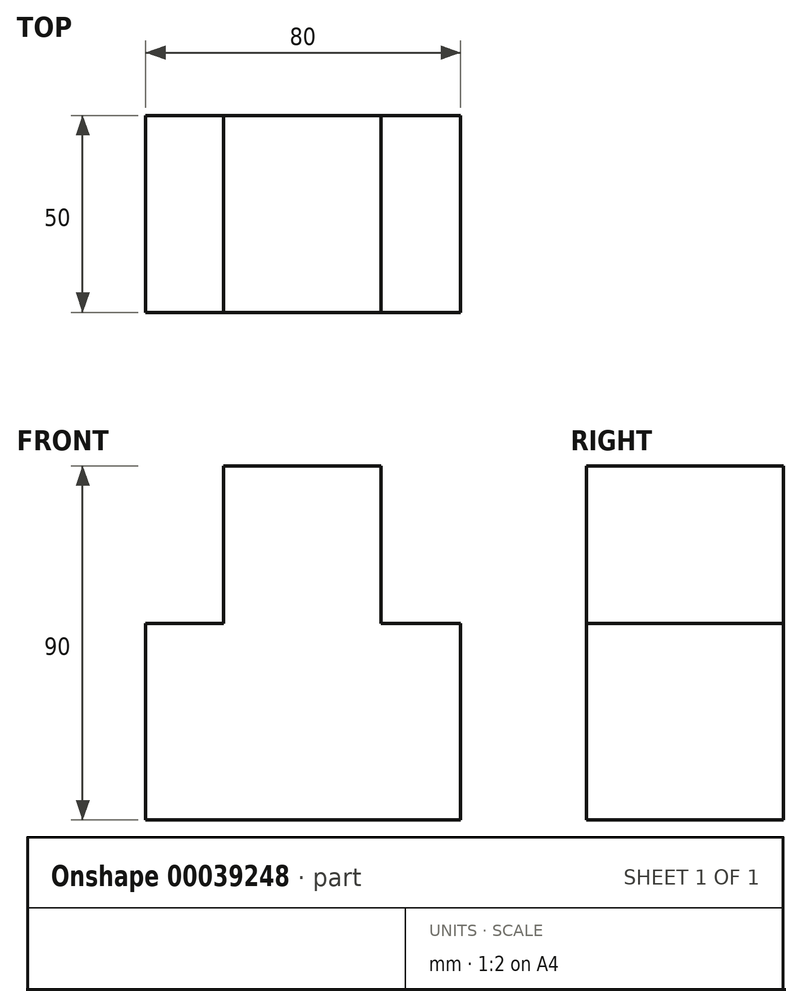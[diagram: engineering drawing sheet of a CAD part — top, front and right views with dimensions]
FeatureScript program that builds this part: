
annotation { "Feature Type Name" : "Feature", "Feature Type Description" : "" }
export const myFeature = defineFeature(function(context is Context, id is Id, definition is map)
    precondition{}
    {
        {
            var Q0;
            Q0=qCreatedBy(makeId("Front.planeOp"),FACE);
            var sketch = newSketch(context, id + "F0", { "sketchPlane" : qUnion([Q0])});
            skLineSegment(sketch, "E0.bottom", {"start": v(-38.96, 31.17) * mm, "end": v(-19.19, 31.17) * mm});
            skLineSegment(sketch, "E0.top", {"start": v(-38.96, -18.83) * mm, "end": v(41.04, -18.83) * mm});
            skLineSegment(sketch, "E0.left", {"start": v(-38.96, 31.17) * mm, "end": v(-38.96, -18.83) * mm});
            skLineSegment(sketch, "E0.right", {"start": v(41.04, 31.17) * mm, "end": v(41.04, -18.83) * mm});
            skLineSegment(sketch, "E1.bottom", {"start": v(-19.19, 71.17) * mm, "end": v(20.81, 71.17) * mm});
            skLineSegment(sketch, "E1.left", {"start": v(-19.19, 71.17) * mm, "end": v(-19.19, 31.17) * mm});
            skLineSegment(sketch, "E1.right", {"start": v(20.81, 71.17) * mm, "end": v(20.81, 31.17) * mm});
            skLineSegment(sketch, "E2.trimOffspring", {"start": v(20.81, 31.17) * mm, "end": v(41.04, 31.17) * mm});
            skSolve(sketch);
        }
        {
            var Q0;
            Q0=makeQuery(id+"F0.imprint","IMPRINT",FACE,{"disambiguationData":[TD([[makeQuery(id+"F0.imprint","IMPRINT",EDGE,{"derivedFrom":sQuery(id+"F0.wireOp",EDGE,"E0.bottom")}),-1.0]])]});
            extrude(context, id + "F1", {"entities" : qUnion([Q0]), "depth" : 50 * mm});
        }
    });
